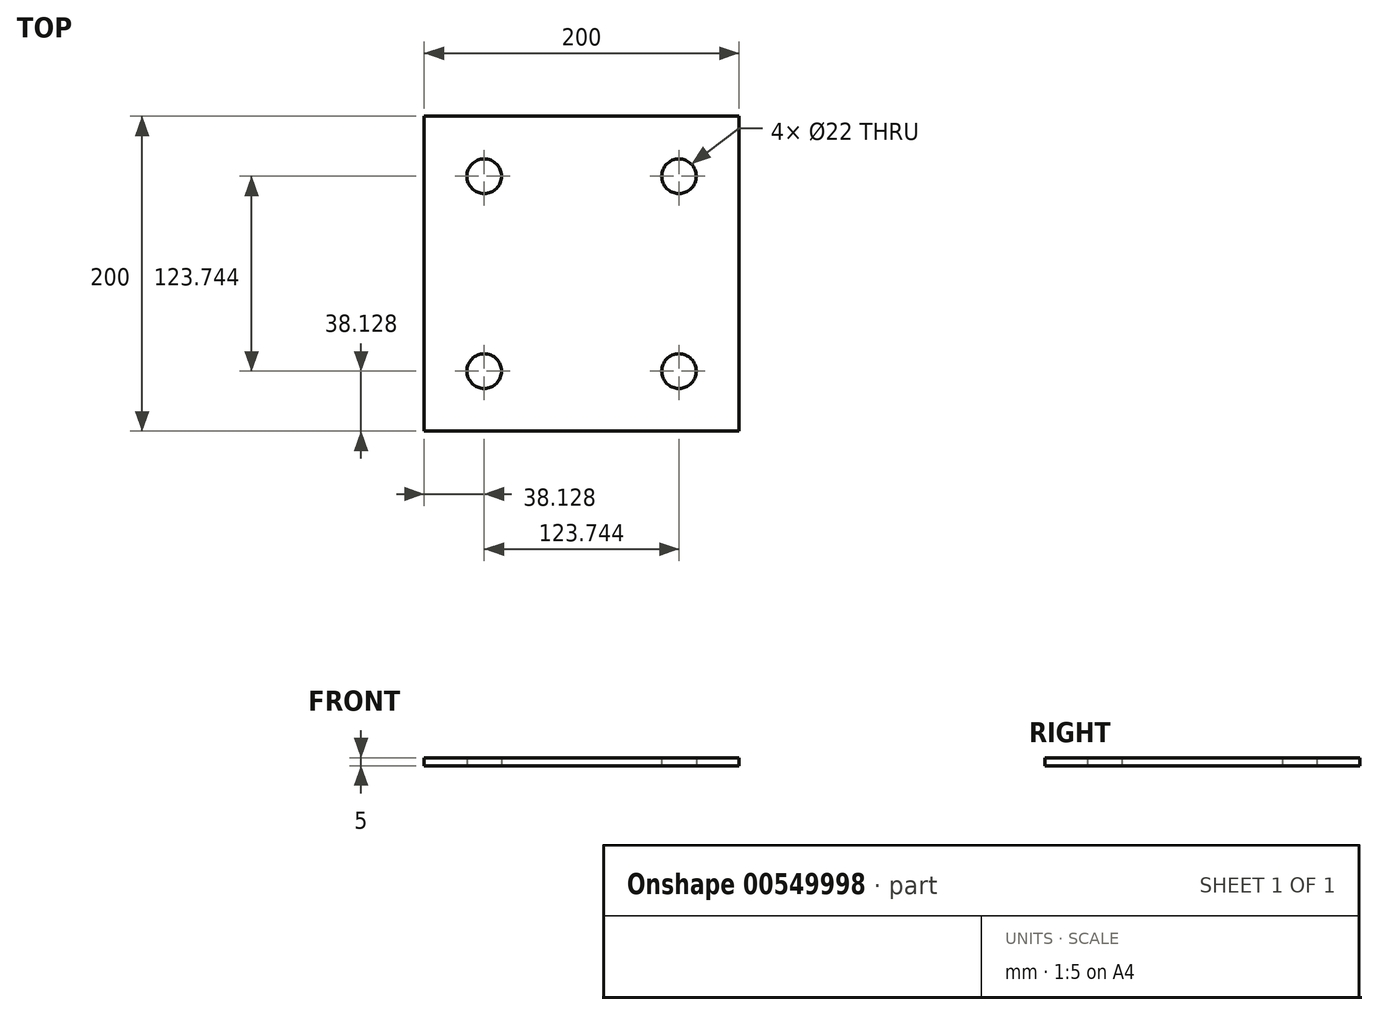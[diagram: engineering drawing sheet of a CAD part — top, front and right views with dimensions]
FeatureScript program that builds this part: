
annotation { "Feature Type Name" : "Feature", "Feature Type Description" : "" }
export const myFeature = defineFeature(function(context is Context, id is Id, definition is map)
    precondition{}
    {
        {
            var Q0;
            Q0=qCreatedBy(makeId("Top.planeOp"),FACE);
            var sketch = newSketch(context, id + "F0", { "sketchPlane" : qUnion([Q0])});
            skLineSegment(sketch, "E0.bottom", {"start": v(100, 100) * mm, "end": v(-100, 100) * mm});
            skLineSegment(sketch, "E0.top", {"start": v(100, -100) * mm, "end": v(-100, -100) * mm});
            skLineSegment(sketch, "E0.left", {"start": v(100, 100) * mm, "end": v(100, -100) * mm});
            skLineSegment(sketch, "E0.right", {"start": v(-100, 100) * mm, "end": v(-100, -100) * mm});
            skLineSegment(sketch, "E1", {"start": v(100, -100) * mm, "end": v(-100, 100) * mm, "construction": true});
            skCircle(sketch, "E2", {"center": v(-61.87, 61.87) * mm, "radius": 11 * mm});
            skCircle(sketch, "E3", {"center": v(61.87, 61.87) * mm, "radius": 11 * mm});
            skCircle(sketch, "E4", {"center": v(-61.87, -61.87) * mm, "radius": 11 * mm});
            skCircle(sketch, "E5", {"center": v(61.87, -61.87) * mm, "radius": 11 * mm});
            skLineSegment(sketch, "E6", {"start": v(-61.87, -61.87) * mm, "end": v(61.87, 61.87) * mm, "construction": true});
            skCircle(sketch, "E7", {"center": v(0, 0) * mm, "radius": 87.5 * mm, "construction": true});
            skSolve(sketch);
        }
        {
            var Q0;
            Q0 = qSketchRegion(id + "F0", true);
            extrude(context, id + "F1", {"entities" : qUnion([Q0]), "depth" : 5 * mm, "offsetDistance" : 25 * mm});
        }
    });
